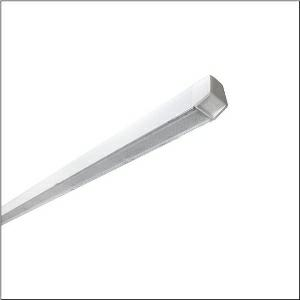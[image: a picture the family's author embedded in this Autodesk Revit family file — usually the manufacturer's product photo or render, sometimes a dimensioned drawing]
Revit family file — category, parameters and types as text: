
# Revit family: licross_r__21_recessed_ho_52ul1edv4d5f00s_4953
name_source: partatom
category: Lighting Fixtures
units: mm (PartAtom-declared; Revit-internal decimal feet)

## family parameters
Cut with Voids When Loaded = No
Host = Face
Light Source = No
Part Type = Normal
Room Calculation Point = No
Round Connector Dimension = Use Diameter
Shared = No

## types (1)
- --- (1 x LED, 13820 lm, 87.2 W, 4000K)
    Apparent Load = 87 VA
    CIE Flux Codes = 85 95 99 100 100
    Color Rendering = 80
    Color Temperature = 4000K
    Default Elevation = 1800 mm
    Description = Licross® 21 Recessed HO, single luminaire, primary optical cover: cover, of PMMA, light emission: direct distribution, installation type: slip-in mounting, LED, rated luminous flux: 13.820lm, luminous efficacy: 159lm/W, light colour: 840, colour temperature: 4000K, control gear: ECG DALI, with terminal, 5-pole, max. 2.5mm², mains connection: 230V, AC, 50/60Hz, rated input power: 87W, Licross® LED insert, of sheet steel, galvanised, coil coated, white, length: 2.327mm, width: 70mm, height: 71mm, end cap, of PC, white, mounting rail, of sheet steel, galvanised, white, protection rating (complete): IP20, insulation class (complete): insulation class I (protective earthing), certification: CE, ENEC, VDE, UKCA, impact resistance: IK06, permissible operating ambient temperature: -25..+35°C, corresponds to IFS (International Featured Standards) requirements for safety and quality in the food industry, reducing of maximum allowable ambient temperature of 5°C with ceiling mounting, LABS conformity tested according to VDMA 24364:2018-05, packaging unit: 1 piece
    Height = 58 mm
    Lamp = 1 x LED
    Lamp Light Flux = 13820 lm
    Lamp Power = 87.2 W
    Lamp count = 1
    Length = 2250 mm
    Luminous efficacy = 158 lm/W
    Manufacturer = Siteco
    ModVariant = No
    Model = 52UL1EDV4D5F00S
    Mounting Place = Ceiling
    Mounting Type = Pendant
    Number of Poles = 1
    OnlyDefault = Yes
    Power Factor = 1
    Product Name = Licross® 21 Recessed HO
    Product group = single luminaire
    ProductGroupID = 909
    Protection Class = Protection class I
    Protection Degree = IP 20
    RLX_Detail_Level = 1
    RlxData = <blob elided: 31825 chars, md5=282752a8>
    Socket = socket
    Standby Power = 0 W
    System Light Flux = 13820 lm
    System Power = 87 W
    Type Comments = factory setting: luminous flux: 100 % | dim-lin: 254 | 405 mA
    Type Image = l_1006979.jpg
    URL = http://relux.com
    VarID = @adj_092713
    Voltage = 0 V
    Weight = 0.00 kg
    Width = 66 mm

## geometry (parser evidence)
native form markers: Blend x4, Sweep x11
no freeform markers — native parametric forms only
